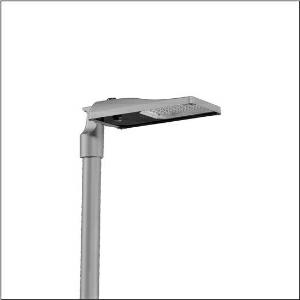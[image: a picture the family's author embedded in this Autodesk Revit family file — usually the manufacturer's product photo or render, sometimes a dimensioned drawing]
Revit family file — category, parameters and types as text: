
# Revit family: streetlight_sl_31_mini___st0_5a_5xh6b31t08ha_d023
name_source: partatom
category: Lighting Fixtures
units: mm (PartAtom-declared; Revit-internal decimal feet)

## family parameters
Cut with Voids When Loaded = No
Host = Face
Light Source = No
Part Type = Normal
Room Calculation Point = No
Round Connector Dimension = Use Diameter
Shared = No

## types (1)
- --- (1 x LED, 9230 lm, 68.3 W, 3000K)
    Apparent Load = 68 VA
    CIE Flux Codes = 41 75 97 100 100
    Color Rendering = 70
    Color Temperature = 3000K
    Default Elevation = 1800 mm
    Description = Streetlight SL 31 mini D4i, Desk-Remote mast luminaire for post-top, side-entry; light control with lens of PMMA; light distribution: ST0.5a, direct asymmetric distribution, for standard-compliant lighting for roads and squares; LED: luminous flux: 9.230lm, light colour: 730, colour temperature: 3000K; luminous efficacy: 135,1lm/W; control: pre-setting: logarithmic dimming characteristic, flexible luminous flux parameterisation, time-dependent luminous flux control, constant luminous flux control, power reduction, intelligent temperature release in ECG and LED module, overheat protection; luminaire housing, of diecast aluminium, SITECO metallic grey (DB 702S), corrosivity category C5 high according to DIN EN ISO 12944; cover of toughened safety glass, transparent, opened without tools; mast flange of diecast aluminium, SITECO metallic grey (DB 702S), spigot size: 76/60mm, mast flange included unmounted; with cable H07RN-F 2x 1.5mm², cable length: 8,5m, connection cable pre-assembled; mains connection: 220..240V, AC, 50/60Hz; power consumption (at start of service life): 68,3W / (at end of service life): 74,5W / (with reduced operation 50%): 29,5W; protection rating (complete): IP66; insulation class (complete): insulation class II (safety insulation); impact resistance: IK09; certification: CE, ENEC, ENEC+, VDE, UKCA, ZD4i; permissible operating ambient temperature for outdoor applications: -40..+50°C; packaging unit: 1 piece

Light Distribution: ST0.5a
    Height = 76 mm
    Lamp = 1 x LED
    Lamp Light Flux = 9230 lm
    Lamp Power = 68.3 W
    Lamp count = 1
    Length = 547 mm
    Luminous efficacy = 135 lm/W
    Manufacturer = Siteco
    ModVariant = No
    Model = 5XH6B31T08HA
    Number of Poles = 1
    OnlyDefault = Yes
    Power Factor = 1
    Product Name = Streetlight SL 31 mini | ST0.5a
    Product group = mast luminaire | pylon top
    ProductGroupID = 6100
    Protection Class = Protection class II
    Protection Degree = IP 66
    RLX_Detail_Level = 1
    RLX_Emergency_Light_Flux = 0 lm
    RLX_Emergency_Type = 0
    RLX_Emergency_Type_DB = No
    RlxData = <blob elided: 35345 chars, md5=c8b18a72>
    Socket = socket
    Standby Power = 0 W
    System Light Flux = 9230 lm
    System Power = 68 W
    Type Comments = factory setting: luminous flux: 100 % | dim-lin: 254 | 692 mA
    Type Image = l_1300332.jpg
    URL = http://relux.com
    VarID = @adj_020815
    Voltage = 0 V
    Weight = 0.00 kg
    Width = 265 mm

## geometry (parser evidence)
native form markers: Blend x4, Sweep x9
no freeform markers — native parametric forms only
